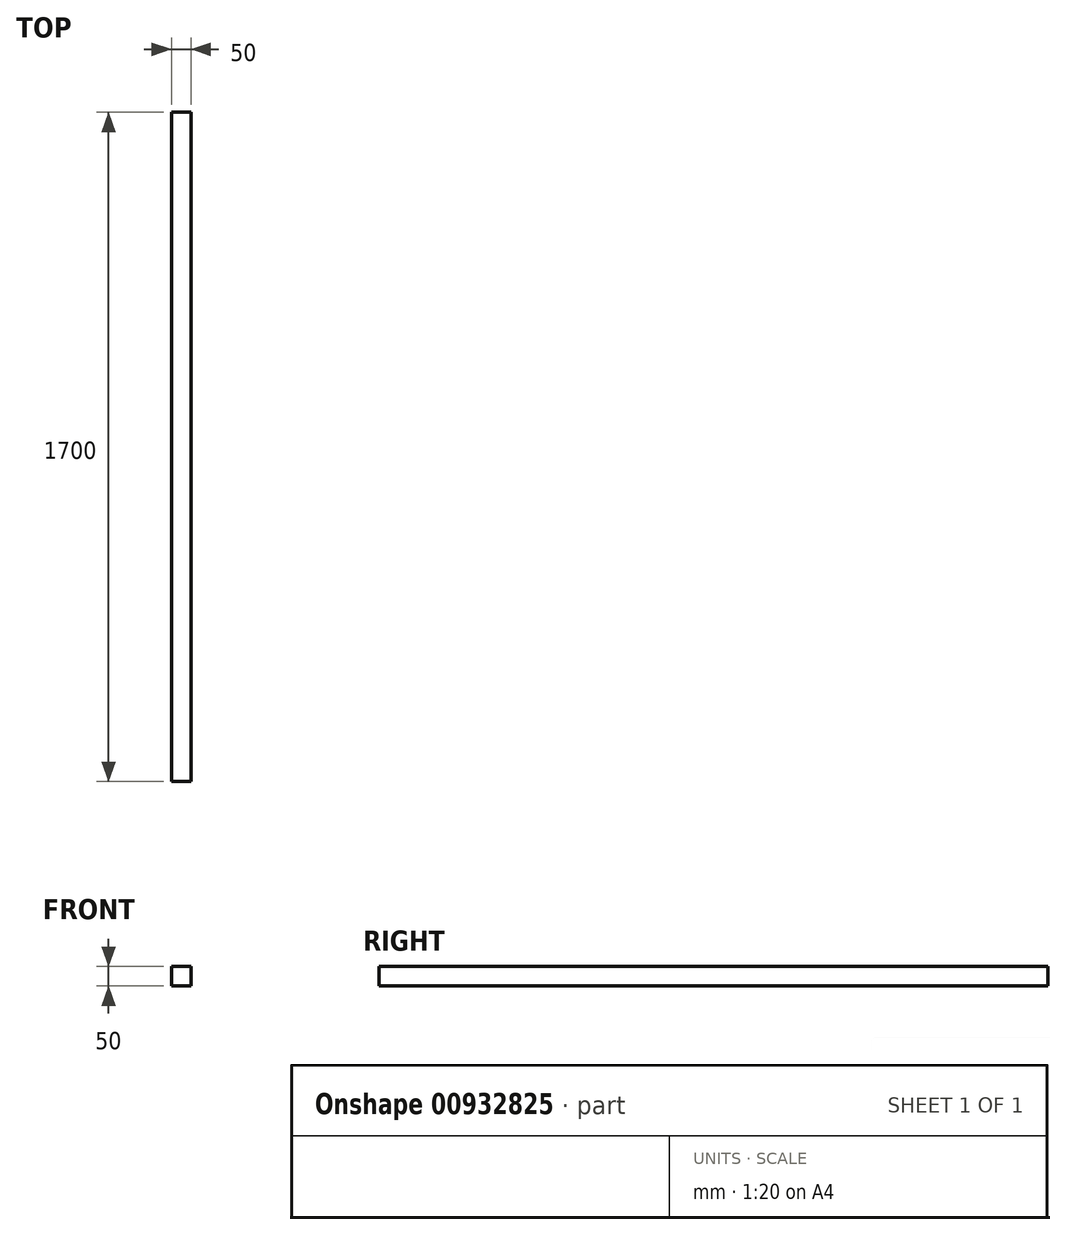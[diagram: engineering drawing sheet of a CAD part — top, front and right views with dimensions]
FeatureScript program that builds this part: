
annotation { "Feature Type Name" : "Feature", "Feature Type Description" : "" }
export const myFeature = defineFeature(function(context is Context, id is Id, definition is map)
    precondition{}
    {
        {
            var Q0;
            Q0=qCreatedBy(makeId("Front.planeOp"),FACE);
            var sketch = newSketch(context, id + "F0", { "sketchPlane" : qUnion([Q0])});
            skLineSegment(sketch, "E0.bottom", {"start": v(25, 25) * mm, "end": v(-25, 25) * mm});
            skLineSegment(sketch, "E0.top", {"start": v(25, -25) * mm, "end": v(-25, -25) * mm});
            skLineSegment(sketch, "E0.left", {"start": v(25, 25) * mm, "end": v(25, -25) * mm});
            skLineSegment(sketch, "E0.right", {"start": v(-25, 25) * mm, "end": v(-25, -25) * mm});
            skPoint(sketch, "E0.middle", {"position": v(0, 0) * mm});
            skSolve(sketch);
        }
        {
            var Q0;
            Q0 = qSketchRegion(id + "F0", true);
            extrude(context, id + "F1", {"entities" : qUnion([Q0]), "depth" : 1700 * mm, "offsetDistance" : 25 * mm, "symmetric" : true});
        }
    });
